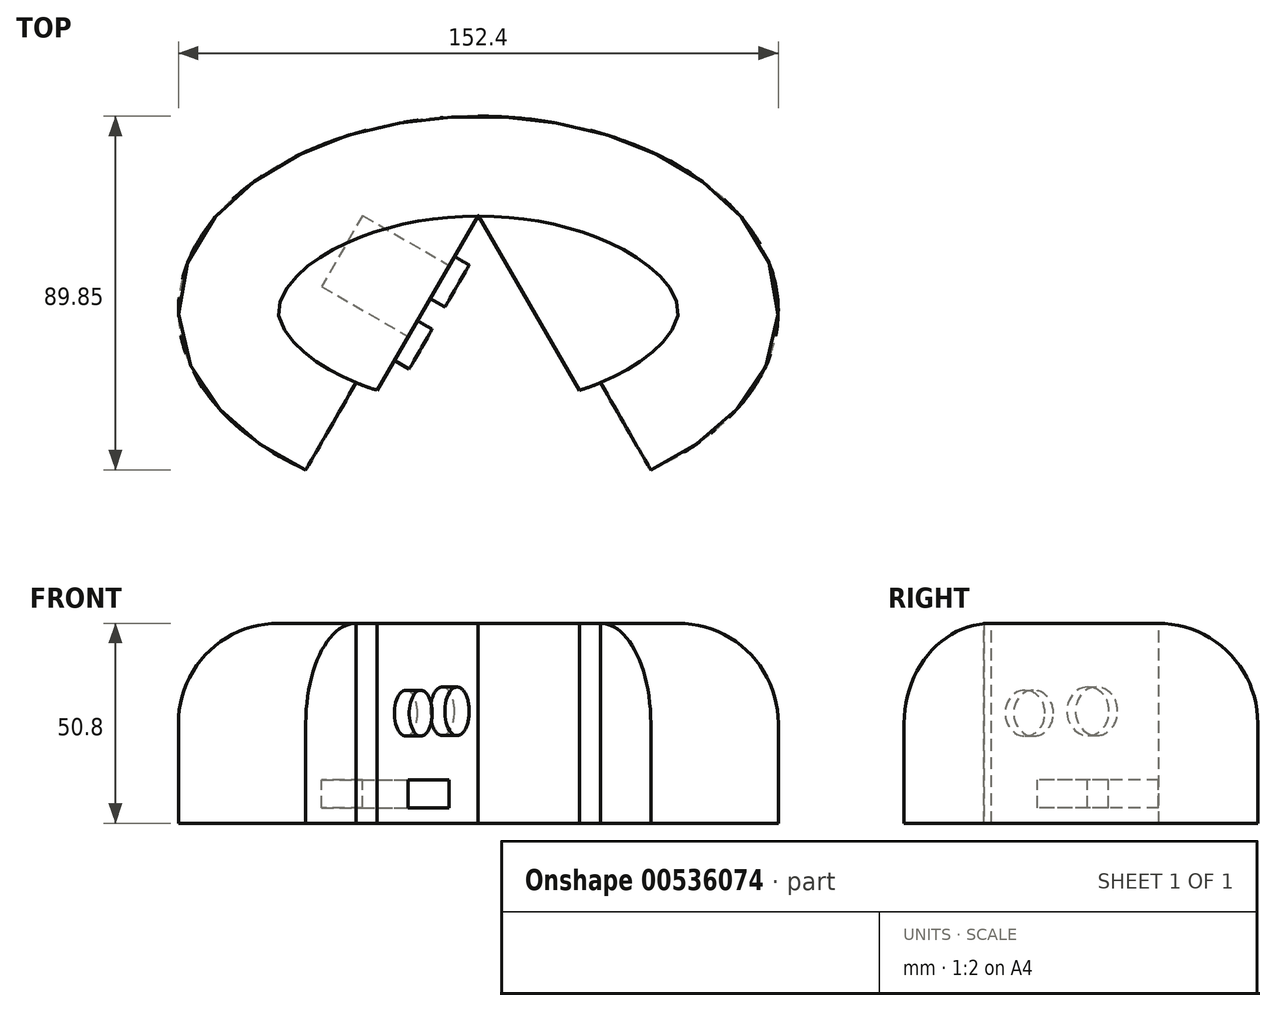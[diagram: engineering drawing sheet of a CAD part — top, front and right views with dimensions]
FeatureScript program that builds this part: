
annotation { "Feature Type Name" : "Feature", "Feature Type Description" : "" }
export const myFeature = defineFeature(function(context is Context, id is Id, definition is map)
    precondition{}
    {
        {
            var Q0;
            Q0=qCreatedBy(makeId("Top.planeOp"),FACE);
            var sketch = newSketch(context, id + "F0", { "sketchPlane" : qUnion([Q0])});
            skEllipse(sketch, "E0", {"center": v(0, 0) * mm, "majorRadius": 76.2 * mm, "minorRadius": 49.42 * mm, "majorAxis": v(1, 0)});
            skSolve(sketch);
        }
        {
            var Q0;
            Q0=makeQuery(id+"F0.imprint","IMPRINT",FACE,{"disambiguationData":[TD([[makeQuery(id+"F0.imprint","IMPRINT",EDGE,{"derivedFrom":sQuery(id+"F0.wireOp",EDGE,"E0")}),1.0]])]});
            extrude(context, id + "F1", {"entities" : qUnion([Q0]), "depth" : 25.4 * mm, "offsetDistance" : 25.4 * mm});
        }
        {
            var Q0;
            Q0=makeQuery(id+"F1.opExtrude","CAP_FACE",FACE,{"disambiguationData":[OSD([sQuery(id+"F0.wireOp",EDGE,"E0")])],"isStart":true});
            extrude(context, id + "F2", {"entities" : qUnion([Q0]), "operationType" : NewBodyOperationType.ADD, "depth" : 25.4 * mm, "offsetDistance" : 25.4 * mm});
        }
        {
            var Q0;
            Q0=makeQuery(id+"F1.opExtrude","CAP_EDGE",EDGE,{"disambiguationData":[OSD([sQuery(id+"F0.wireOp",EDGE,"E0")])],"isStart":false});
            fillet(context, id + "F3", {"entities" : qUnion([Q0]), "radius" : 25.4 * mm, "tangentPropagation" : true, "allowEdgeOverflow" : false});
        }
        {
            var Q0;
            Q0=makeQuery(id+"F1.opExtrude","CAP_FACE",FACE,{"disambiguationData":[OSD([sQuery(id+"F0.wireOp",EDGE,"E0")])],"isStart":false});
            var sketch = newSketch(context, id + "F4", { "sketchPlane" : qUnion([Q0])});
            skCircle(sketch, "E1.cCircle", {"center": v(0, -35.14) * mm, "radius": 35.3 * mm, "construction": true});
            skLineSegment(sketch, "E1.0", {"start": v(61.15, -70.44) * mm, "end": v(-61.15, -70.44) * mm});
            skLineSegment(sketch, "E1.1", {"start": v(-61.15, -70.44) * mm, "end": v(0, 35.47) * mm});
            skLineSegment(sketch, "E1.2", {"start": v(0, 35.47) * mm, "end": v(61.15, -70.44) * mm});
            skPoint(sketch, "E1.0.midPoint", {"position": v(0, -70.44) * mm});
            skSolve(sketch);
        }
        {
            var Q0;
            {var subQ0=sQuery(id+"F4.wireOp",EDGE,"E1.0");Q0=makeQuery(id+"F4.imprint","IMPRINT",FACE,{"disambiguationData":[TD([[makeQuery(id+"F4.imprint","IMPRINT",EDGE,{"derivedFrom":subQ0}),-1.0]])]});}
            extrude(context, id + "F5", {"entities" : qUnion([Q0]), "operationType" : NewBodyOperationType.REMOVE, "oppositeDirection" : true, "depth" : 76.2 * mm, "offsetDistance" : 25.4 * mm});
        }
        {
            var Q0;
            Q0=makeQuery(id+"F1.opExtrude","CAP_FACE",FACE,{"disambiguationData":[OSD([sQuery(id+"F0.wireOp",EDGE,"E0")])],"isStart":false});
            var sketch = newSketch(context, id + "F6", { "sketchPlane" : qUnion([Q0])});
            skCircle(sketch, "E2.cCircle", {"center": v(0, -24.02) * mm, "radius": 24.13 * mm, "construction": true});
            skLineSegment(sketch, "E2.0", {"start": v(41.8, -48.15) * mm, "end": v(-41.8, -48.15) * mm});
            skLineSegment(sketch, "E2.1", {"start": v(-41.8, -48.15) * mm, "end": v(0, 24.24) * mm});
            skLineSegment(sketch, "E2.2", {"start": v(0, 24.24) * mm, "end": v(41.8, -48.15) * mm});
            skPoint(sketch, "E2.0.midPoint", {"position": v(0, -48.15) * mm});
            skSolve(sketch);
        }
        {
            var Q0;
            {var subQ0=sQuery(id+"F6.wireOp",EDGE,"E2.2");var subQ1=sQuery(id+"F6.wireOp",EDGE,"E2.1");var subQ2=makeQuery(id+"F6.imprint","INTERSECT",VERTEX,{"derivedFrom":[subQ1,subQ0]});Q0=makeQuery(id+"F6.imprint","IMPRINT",FACE,{"disambiguationData":[TD([[makeQuery(id+"F6.imprint","IMPRINT",EDGE,{"disambiguationData":[TD([[subQ2,1.0]])],"derivedFrom":subQ1}),-1.0]])]});}
            var Q1;
            {var subQ0=sQuery(id+"F6.wireOp",EDGE,"E2.1");var subQ1=sQuery(id+"F0.wireOp",EDGE,"E0");var subQ2=makeQuery(id+"F3.opFillet","BLEND_EDGE",EDGE,{"blendedFrom":[makeQuery(id+"F1.opExtrude","CAP_EDGE",EDGE,{"disambiguationData":[OSD([subQ1])],"isStart":false}),makeQuery(id+"F1.opExtrude","CAP_FACE",FACE,{"disambiguationData":[OSD([subQ1])],"isStart":false})],"blendedInto":[makeQuery(id+"F1.opExtrude","CAP_FACE",FACE,{"disambiguationData":[OSD([subQ1])],"isStart":false})]});var subQ5=makeQuery(id+"F5.boolean.opBoolean","SPLIT",EDGE,{"derivedFrom":subQ2});var subQ6=makeQuery(id+"F6.imprint","INTERSECT",VERTEX,{"derivedFrom":[subQ5,subQ0]});Q1=makeQuery(id+"F6.imprint","IMPRINT",FACE,{"disambiguationData":[TD([[makeQuery(id+"F6.imprint","IMPRINT",EDGE,{"disambiguationData":[TD([[subQ6,1.0]])],"derivedFrom":subQ0}),-1.0]])]});}
            extrude(context, id + "F7", {"entities" : qUnion([Q0, Q1]), "operationType" : NewBodyOperationType.REMOVE, "oppositeDirection" : true, "depth" : 76.2 * mm, "offsetDistance" : 25.4 * mm});
        }
        {
            var Q0;
            Q0=makeQuery(id+"F7.boolean.opBoolean","COPY",FACE,{"derivedFrom":makeQuery(id+"F7.opExtrude","SWEPT_FACE",FACE,{"disambiguationData":[OSD([sQuery(id+"F6.wireOp",EDGE,"E2.1")])]})});
            var sketch = newSketch(context, id + "F8", { "sketchPlane" : qUnion([Q0])});
            skCircle(sketch, "E3", {"center": v(-15.74, 2.58) * mm, "radius": 5.82 * mm});
            skCircle(sketch, "E4", {"center": v(2.73, 3.05) * mm, "radius": 6.17 * mm});
            skLineSegment(sketch, "E5.bottom", {"start": v(8.8, -12.69) * mm, "end": v(-18.11, -12.69) * mm});
            skLineSegment(sketch, "E5.top", {"start": v(8.8, -20.22) * mm, "end": v(-18.11, -20.22) * mm});
            skLineSegment(sketch, "E5.left", {"start": v(8.8, -12.69) * mm, "end": v(8.8, -20.22) * mm});
            skLineSegment(sketch, "E5.right", {"start": v(-18.11, -12.69) * mm, "end": v(-18.11, -20.22) * mm});
            skPoint(sketch, "E5.middle", {"position": v(-4.66, -16.45) * mm});
            skSolve(sketch);
        }
        {
            var Q0;
            Q0=makeQuery(id+"F8.imprint","IMPRINT",FACE,{"disambiguationData":[TD([[makeQuery(id+"F8.imprint","IMPRINT",EDGE,{"derivedFrom":sQuery(id+"F8.wireOp",EDGE,"E3")}),1.0]])]});
            var Q1;
            Q1=makeQuery(id+"F8.imprint","IMPRINT",FACE,{"disambiguationData":[TD([[makeQuery(id+"F8.imprint","IMPRINT",EDGE,{"derivedFrom":sQuery(id+"F8.wireOp",EDGE,"E4")}),1.0]])]});
            extrude(context, id + "F9", {"entities" : qUnion([Q0, Q1]), "operationType" : NewBodyOperationType.ADD, "depth" : 4.32 * mm, "offsetDistance" : 25.4 * mm});
        }
        {
            var Q0;
            Q0=makeQuery(id+"F7.boolean.opBoolean","COPY",FACE,{"derivedFrom":makeQuery(id+"F7.opExtrude","SWEPT_FACE",FACE,{"disambiguationData":[OSD([sQuery(id+"F6.wireOp",EDGE,"E2.1")])]})});
            var sketch = newSketch(context, id + "F10", { "sketchPlane" : qUnion([Q0])});
            skLineSegment(sketch, "E6.bottom", {"start": v(6.26, -21.46) * mm, "end": v(-14.6, -21.46) * mm});
            skLineSegment(sketch, "E6.top", {"start": v(6.26, -14.4) * mm, "end": v(-14.6, -14.4) * mm});
            skLineSegment(sketch, "E6.left", {"start": v(6.26, -21.46) * mm, "end": v(6.26, -14.4) * mm});
            skLineSegment(sketch, "E6.right", {"start": v(-14.6, -21.46) * mm, "end": v(-14.6, -14.4) * mm});
            skPoint(sketch, "E6.middle", {"position": v(-4.17, -17.93) * mm});
            skSolve(sketch);
        }
        {
            var Q0;
            Q0 = qSketchRegion(id + "F10", true);
            extrude(context, id + "F11", {"entities" : qUnion([Q0]), "operationType" : NewBodyOperationType.REMOVE, "oppositeDirection" : true, "depth" : 25.4 * mm, "offsetDistance" : 25.4 * mm});
        }
    });
